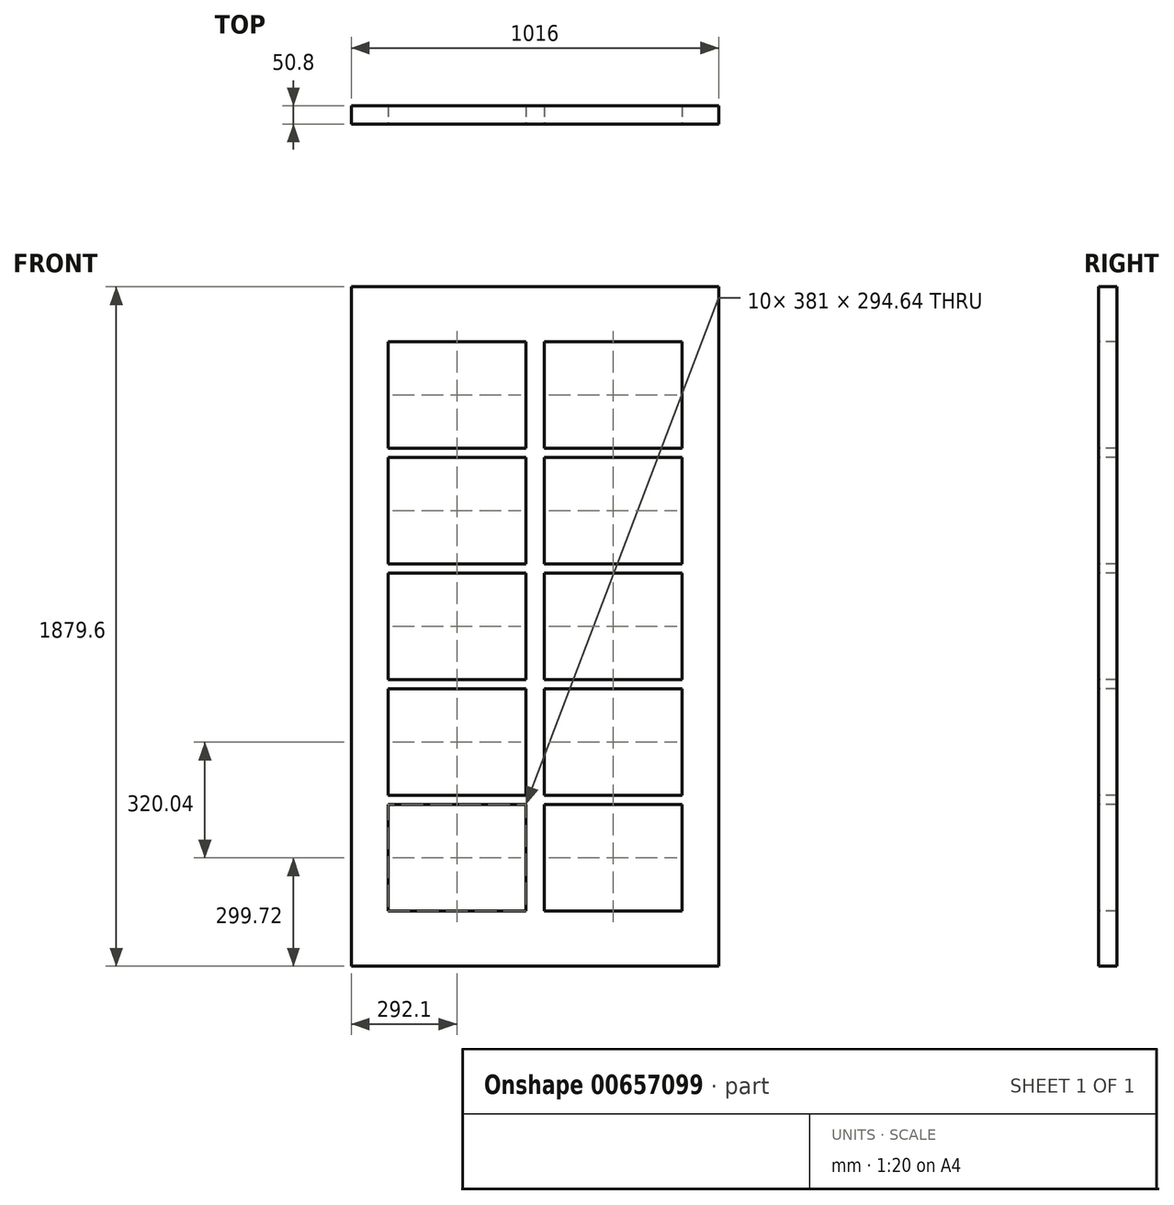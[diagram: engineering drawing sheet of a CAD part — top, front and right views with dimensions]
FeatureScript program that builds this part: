
annotation { "Feature Type Name" : "Feature", "Feature Type Description" : "" }
export const myFeature = defineFeature(function(context is Context, id is Id, definition is map)
    precondition{}
    {
        {
            var Q0;
            Q0=qCreatedBy(makeId("Front.planeOp"),FACE);
            var sketch = newSketch(context, id + "F0", { "sketchPlane" : qUnion([Q0])});
            skLineSegment(sketch, "E0.bottom", {"start": v(-508, 939.8) * mm, "end": v(508, 939.8) * mm});
            skLineSegment(sketch, "E0.top", {"start": v(-508, -939.8) * mm, "end": v(508, -939.8) * mm});
            skLineSegment(sketch, "E0.left", {"start": v(-508, 939.8) * mm, "end": v(-508, -939.8) * mm});
            skLineSegment(sketch, "E0.right", {"start": v(508, 939.8) * mm, "end": v(508, -939.8) * mm});
            skSolve(sketch);
        }
        {
            var Q0;
            Q0 = qSketchRegion(id + "F0", true);
            extrude(context, id + "F1", {"entities" : qUnion([Q0]), "depth" : 50.8 * mm, "offsetDistance" : 25.4 * mm});
        }
        {
            var Q0;
            Q0=makeQuery(id+"F1.opExtrude","CAP_FACE",FACE,{"disambiguationData":[OSD([sQuery(id+"F0.wireOp",EDGE,"E0.bottom"),sQuery(id+"F0.wireOp",EDGE,"E0.top"),sQuery(id+"F0.wireOp",EDGE,"E0.left"),sQuery(id+"F0.wireOp",EDGE,"E0.right")])],"isStart":false});
            var sketch = newSketch(context, id + "F2", { "sketchPlane" : qUnion([Q0])});
            skLineSegment(sketch, "E1.bottom", {"start": v(-406.4, 787.4) * mm, "end": v(-25.4, 787.4) * mm});
            skLineSegment(sketch, "E1.top", {"start": v(-406.4, 492.76) * mm, "end": v(-25.4, 492.76) * mm});
            skLineSegment(sketch, "E1.left", {"start": v(-406.4, 787.4) * mm, "end": v(-406.4, 492.76) * mm});
            skLineSegment(sketch, "E1.right", {"start": v(-25.4, 787.4) * mm, "end": v(-25.4, 492.76) * mm});
            skLineSegment(sketch, "E2.bottom", {"start": v(-406.4, 467.36) * mm, "end": v(-25.4, 467.36) * mm});
            skLineSegment(sketch, "E2.top", {"start": v(-406.4, 172.72) * mm, "end": v(-25.4, 172.72) * mm});
            skLineSegment(sketch, "E2.left", {"start": v(-406.4, 467.36) * mm, "end": v(-406.4, 172.72) * mm});
            skLineSegment(sketch, "E2.right", {"start": v(-25.4, 467.36) * mm, "end": v(-25.4, 172.72) * mm});
            skLineSegment(sketch, "E3.bottom", {"start": v(-406.4, 147.32) * mm, "end": v(-25.4, 147.32) * mm});
            skLineSegment(sketch, "E3.top", {"start": v(-406.4, -147.32) * mm, "end": v(-25.4, -147.32) * mm});
            skLineSegment(sketch, "E3.left", {"start": v(-406.4, 147.32) * mm, "end": v(-406.4, -147.32) * mm});
            skLineSegment(sketch, "E3.right", {"start": v(-25.4, 147.32) * mm, "end": v(-25.4, -147.32) * mm});
            skLineSegment(sketch, "E4.bottom", {"start": v(-406.4, -172.72) * mm, "end": v(-25.4, -172.72) * mm});
            skLineSegment(sketch, "E4.top", {"start": v(-406.4, -467.36) * mm, "end": v(-25.4, -467.36) * mm});
            skLineSegment(sketch, "E4.left", {"start": v(-406.4, -172.72) * mm, "end": v(-406.4, -467.36) * mm});
            skLineSegment(sketch, "E4.right", {"start": v(-25.4, -172.72) * mm, "end": v(-25.4, -467.36) * mm});
            skLineSegment(sketch, "E5.bottom", {"start": v(-406.4, -492.76) * mm, "end": v(-25.4, -492.76) * mm});
            skLineSegment(sketch, "E5.top", {"start": v(-406.4, -787.4) * mm, "end": v(-25.4, -787.4) * mm});
            skLineSegment(sketch, "E5.left", {"start": v(-406.4, -492.76) * mm, "end": v(-406.4, -787.4) * mm});
            skLineSegment(sketch, "E5.right", {"start": v(-25.4, -492.76) * mm, "end": v(-25.4, -787.4) * mm});
            skLineSegment(sketch, "E6", {"start": v(-406.4, 492.76) * mm, "end": v(-508, 492.76) * mm, "construction": true});
            skLineSegment(sketch, "E7", {"start": v(-406.4, 172.72) * mm, "end": v(-508, 172.72) * mm, "construction": true});
            skLineSegment(sketch, "E8", {"start": v(-406.4, -147.32) * mm, "end": v(-508, -147.32) * mm, "construction": true});
            skLineSegment(sketch, "E9", {"start": v(-406.4, -467.36) * mm, "end": v(-508, -467.36) * mm, "construction": true});
            skLineSegment(sketch, "E10", {"start": v(-406.4, -787.4) * mm, "end": v(-508, -787.4) * mm, "construction": true});
            skLineSegment(sketch, "E11", {"start": v(0, 939.8) * mm, "end": v(0, -939.8) * mm, "construction": true});
            skLineSegment(sketch, "E12.MirrorCS", {"start": v(406.4, 467.36) * mm, "end": v(406.4, 172.72) * mm});
            skLineSegment(sketch, "E13.MirrorCS", {"start": v(406.4, 172.72) * mm, "end": v(25.4, 172.72) * mm});
            skLineSegment(sketch, "E14.MirrorCS", {"start": v(406.4, 467.36) * mm, "end": v(25.4, 467.36) * mm});
            skLineSegment(sketch, "E15.MirrorCS", {"start": v(25.4, 467.36) * mm, "end": v(25.4, 172.72) * mm});
            skLineSegment(sketch, "E16.MirrorCS", {"start": v(25.4, 787.4) * mm, "end": v(25.4, 492.76) * mm});
            skLineSegment(sketch, "E17.MirrorCS", {"start": v(406.4, 787.4) * mm, "end": v(406.4, 492.76) * mm});
            skLineSegment(sketch, "E18.MirrorCS", {"start": v(406.4, 492.76) * mm, "end": v(25.4, 492.76) * mm});
            skLineSegment(sketch, "E19.MirrorCS", {"start": v(406.4, -147.32) * mm, "end": v(25.4, -147.32) * mm});
            skLineSegment(sketch, "E20.MirrorCS", {"start": v(406.4, 787.4) * mm, "end": v(25.4, 787.4) * mm});
            skLineSegment(sketch, "E21.MirrorCS", {"start": v(25.4, -172.72) * mm, "end": v(25.4, -467.36) * mm});
            skLineSegment(sketch, "E22.MirrorCS", {"start": v(406.4, -172.72) * mm, "end": v(406.4, -467.36) * mm});
            skLineSegment(sketch, "E23.MirrorCS", {"start": v(406.4, 147.32) * mm, "end": v(406.4, -147.32) * mm});
            skLineSegment(sketch, "E24.MirrorCS", {"start": v(25.4, 147.32) * mm, "end": v(25.4, -147.32) * mm});
            skLineSegment(sketch, "E25.MirrorCS", {"start": v(406.4, -172.72) * mm, "end": v(25.4, -172.72) * mm});
            skLineSegment(sketch, "E26.MirrorCS", {"start": v(406.4, -467.36) * mm, "end": v(25.4, -467.36) * mm});
            skLineSegment(sketch, "E27.MirrorCS", {"start": v(406.4, -492.76) * mm, "end": v(406.4, -787.4) * mm});
            skLineSegment(sketch, "E28.MirrorCS", {"start": v(406.4, -492.76) * mm, "end": v(25.4, -492.76) * mm});
            skLineSegment(sketch, "E29.MirrorCS", {"start": v(406.4, -787.4) * mm, "end": v(25.4, -787.4) * mm});
            skLineSegment(sketch, "E30.MirrorCS", {"start": v(25.4, -492.76) * mm, "end": v(25.4, -787.4) * mm});
            skLineSegment(sketch, "E31.MirrorCS", {"start": v(406.4, 147.32) * mm, "end": v(25.4, 147.32) * mm});
            skSolve(sketch);
        }
        {
            var Q0;
            Q0 = qSketchRegion(id + "F2", true);
            extrude(context, id + "F3", {"entities" : qUnion([Q0]), "operationType" : NewBodyOperationType.REMOVE, "endBound" : BoundingType.THROUGH_ALL, "oppositeDirection" : true, "depth" : 25.4 * mm, "offsetDistance" : 25.4 * mm});
        }
    });
